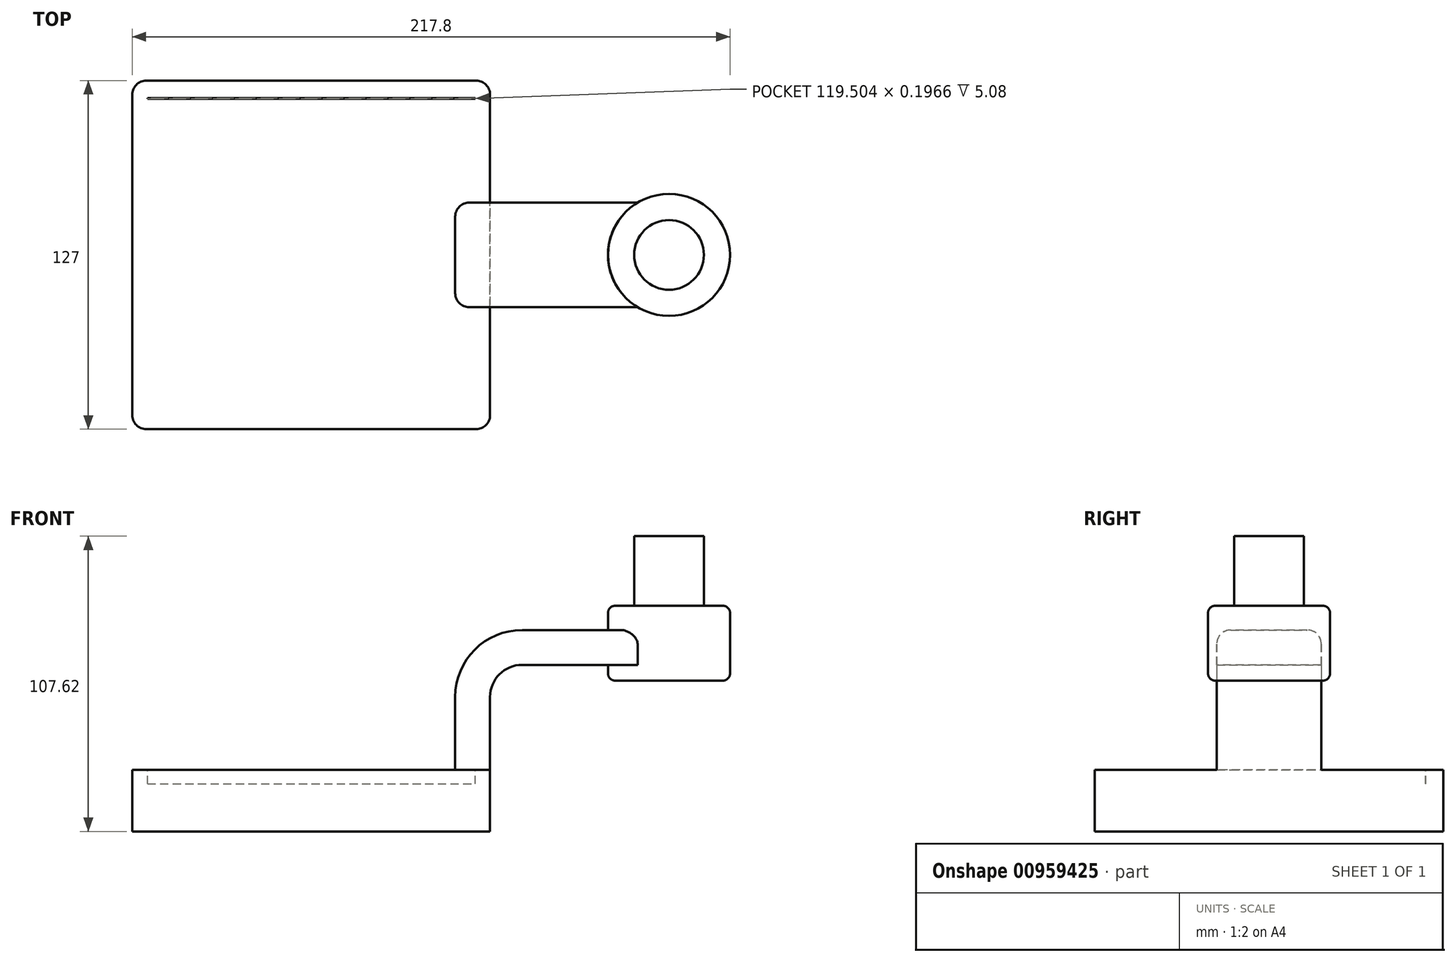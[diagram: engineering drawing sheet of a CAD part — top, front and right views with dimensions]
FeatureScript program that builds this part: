
annotation { "Feature Type Name" : "Feature", "Feature Type Description" : "" }
export const myFeature = defineFeature(function(context is Context, id is Id, definition is map)
    precondition{}
    {
        {
            var Q0;
            Q0=qCreatedBy(makeId("Front.planeOp"),FACE);
            var sketch = newSketch(context, id + "F0", { "sketchPlane" : qUnion([Q0])});
            skLineSegment(sketch, "E0.bottom", {"start": v(-65.2, 11.19) * mm, "end": v(65.2, 11.19) * mm});
            skLineSegment(sketch, "E0.top", {"start": v(-65.2, -11.19) * mm, "end": v(65.2, -11.19) * mm});
            skLineSegment(sketch, "E0.left", {"start": v(-65.2, 11.19) * mm, "end": v(-65.2, -11.19) * mm});
            skLineSegment(sketch, "E0.right", {"start": v(65.2, 11.19) * mm, "end": v(65.2, -11.19) * mm});
            skPoint(sketch, "E0.middle", {"position": v(0, 0) * mm});
            skLineSegment(sketch, "E1.bottom", {"start": v(152.61, 43.79) * mm, "end": v(108.16, 43.79) * mm});
            skLineSegment(sketch, "E1.top", {"start": v(152.61, 71.03) * mm, "end": v(108.16, 71.03) * mm});
            skLineSegment(sketch, "E1.left", {"start": v(152.61, 43.79) * mm, "end": v(152.61, 71.03) * mm});
            skLineSegment(sketch, "E1.right", {"start": v(108.16, 43.79) * mm, "end": v(108.16, 71.03) * mm});
            skPoint(sketch, "E1.middle", {"position": v(130.39, 57.4) * mm});
            skLineSegment(sketch, "E2", {"start": v(65.2, 11.19) * mm, "end": v(65.2, 37.82) * mm});
            skArc(sketch, "E3", {"start": v(65.2, 37.82) * mm, "mid": v(68.62, 46.09) * mm, "end": v(76.88, 49.51) * mm});
            skLineSegment(sketch, "E4", {"start": v(76.88, 49.51) * mm, "end": v(130.39, 49.51) * mm});
            skLineSegment(sketch, "E5.0", {"start": v(76.88, 62.21) * mm, "end": v(130.39, 62.21) * mm});
            skArc(sketch, "E5.1", {"start": v(52.5, 37.82) * mm, "mid": v(59.64, 55.07) * mm, "end": v(76.88, 62.21) * mm});
            skLineSegment(sketch, "E5.2", {"start": v(52.5, 11.19) * mm, "end": v(52.5, 37.82) * mm});
            skFitSpline(sketch, "E6", {"points": [v(-65.2, 11.19) * mm, v(76.88, 62.21) * mm], "startDerivative": vector(116.76, 89.03) * mm, "endDerivative": vector(159.12, -1.65) * mm});
            skPoint(sketch, "E7", {"position": v(130.39, 71.03) * mm});
            skPoint(sketch, "E8", {"position": v(130.39, 43.79) * mm});
            skLineSegment(sketch, "E9", {"start": v(130.39, 71.03) * mm, "end": v(130.39, 43.79) * mm});
            skSolve(sketch);
        }
        {
            var Q0;
            Q0=makeQuery(id+"F0.imprint","IMPRINT",FACE,{"disambiguationData":[TD([[makeQuery(id+"F0.imprint","IMPRINT",EDGE,{"derivedFrom":sQuery(id+"F0.wireOp",EDGE,"E0.top")}),1.0]])]});
            extrude(context, id + "F1", {"entities" : qUnion([Q0]), "endBound" : BoundingType.SYMMETRIC, "oppositeDirection" : true, "depth" : 127 * mm, "offsetDistance" : 25.4 * mm});
        }
        {
            var Q0;
            {var subQ1=sQuery(id+"F0.wireOp",EDGE,"E2");Q0=makeQuery(id+"F0.imprint","IMPRINT",FACE,{"disambiguationData":[TD([[makeQuery(id+"F0.imprint","IMPRINT",EDGE,{"derivedFrom":subQ1}),1.0]])]});}
            var Q1;
            {var subQ0=sQuery(id+"F0.wireOp",EDGE,"E4");var subQ1=sQuery(id+"F0.wireOp",EDGE,"E1.right");var subQ2=makeQuery(id+"F0.imprint","INTERSECT",VERTEX,{"derivedFrom":[subQ1,subQ0]});Q1=makeQuery(id+"F0.imprint","IMPRINT",FACE,{"disambiguationData":[TD([[makeQuery(id+"F0.imprint","IMPRINT",EDGE,{"disambiguationData":[TD([[subQ2,-1.0]])],"derivedFrom":subQ1}),-1.0]])]});}
            extrude(context, id + "F2", {"entities" : qUnion([Q0, Q1]), "operationType" : NewBodyOperationType.ADD, "endBound" : BoundingType.SYMMETRIC, "depth" : 38.1 * mm, "offsetDistance" : 25.4 * mm});
        }
        {
            var Q0;
            Q0=makeQuery(id+"F0.imprint","IMPRINT",FACE,{"disambiguationData":[TD([[makeQuery(id+"F0.imprint","IMPRINT",EDGE,{"derivedFrom":sQuery(id+"F0.wireOp",EDGE,"E5.1")}),1.0]])]});
            var Q1;
            {var subQ0=sQuery(id+"F0.wireOp",EDGE,"E4");var subQ1=sQuery(id+"F0.wireOp",EDGE,"E1.right");var subQ2=makeQuery(id+"F0.imprint","INTERSECT",VERTEX,{"derivedFrom":[subQ1,subQ0]});Q1=makeQuery(id+"F0.imprint","IMPRINT",FACE,{"disambiguationData":[TD([[makeQuery(id+"F0.imprint","IMPRINT",EDGE,{"disambiguationData":[TD([[subQ2,-1.0]])],"derivedFrom":subQ1}),-1.0]])]});}
            extrude(context, id + "F3", {"entities" : qUnion([Q0, Q1]), "operationType" : NewBodyOperationType.ADD, "endBound" : BoundingType.SYMMETRIC, "depth" : 6.35 * mm, "offsetDistance" : 25.4 * mm});
        }
        {
            var Q0;
            {var subQ0=sQuery(id+"F0.wireOp",EDGE,"E1.left");Q0=makeQuery(id+"F0.imprint","IMPRINT",FACE,{"disambiguationData":[TD([[makeQuery(id+"F0.imprint","IMPRINT",EDGE,{"derivedFrom":subQ0}),1.0]])]});}
            var Q1;
            Q1=sQuery(id+"F0.wireOp",EDGE,"E9");
            revolve(context, id + "F4", {"operationType" : NewBodyOperationType.ADD, "surfaceOperationType" : NewSurfaceOperationType.NEW, "entities" : qUnion([Q0]), "axis" : qUnion([Q1]), "revolveType" : RevolveType.FULL});
        }
        {
            var Q0;
            Q0=makeQuery(id+"F1.opExtrude","CAP_EDGE",EDGE,{"disambiguationData":[OSD([sQuery(id+"F0.wireOp",EDGE,"E0.left")])],"isStart":true});
            var Q1;
            Q1=makeQuery(id+"F1.opExtrude","CAP_EDGE",EDGE,{"disambiguationData":[OSD([sQuery(id+"F0.wireOp",EDGE,"E0.right")])],"isStart":true});
            var Q2;
            Q2=makeQuery(id+"F1.opExtrude","CAP_EDGE",EDGE,{"disambiguationData":[OSD([sQuery(id+"F0.wireOp",EDGE,"E0.right")])],"isStart":false});
            var Q3;
            Q3=makeQuery(id+"F1.opExtrude","CAP_EDGE",EDGE,{"disambiguationData":[OSD([sQuery(id+"F0.wireOp",EDGE,"E0.left")])],"isStart":false});
            var Q4;
            Q4=makeQuery(id+"F2.opExtrude","CAP_EDGE",EDGE,{"disambiguationData":[OSD([sQuery(id+"F0.wireOp",EDGE,"E5.2")])],"isStart":true});
            var Q5;
            Q5=makeQuery(id+"F2.opExtrude","CAP_EDGE",EDGE,{"disambiguationData":[OSD([sQuery(id+"F0.wireOp",EDGE,"E5.2")])],"isStart":false});
            fillet(context, id + "F5", {"entities" : qUnion([Q0, Q1, Q2, Q3, Q4, Q5]), "radius" : 5.08 * mm, "tangentPropagation" : true, "allowEdgeOverflow" : false});
        }
        {
            var Q0;
            Q0=makeQuery(id+"F4.opRevolve","SWEPT_EDGE",EDGE,{"disambiguationData":[OSD([sQuery(id+"F0.wireOp",EDGE,"E1.top"),sQuery(id+"F0.wireOp",EDGE,"E1.left")])]});
            fillet(context, id + "F6", {"entities" : qUnion([Q0]), "radius" : 2.54 * mm, "tangentPropagation" : true, "allowEdgeOverflow" : false});
        }
        {
            var Q0;
            Q0=makeQuery(id+"F4.opRevolve","SWEPT_EDGE",EDGE,{"disambiguationData":[OSD([sQuery(id+"F0.wireOp",EDGE,"E1.bottom"),sQuery(id+"F0.wireOp",EDGE,"E1.left")])]});
            fillet(context, id + "F7", {"entities" : qUnion([Q0]), "radius" : 2.54 * mm, "tangentPropagation" : true, "allowEdgeOverflow" : false});
        }
        {
            var Q0;
            Q0=makeQuery(id+"F4.opRevolve","SWEPT_FACE",FACE,{"disambiguationData":[OSD([sQuery(id+"F0.wireOp",EDGE,"E1.top")])]});
            var sketch = newSketch(context, id + "F8", { "sketchPlane" : qUnion([Q0])});
            skCircle(sketch, "E10", {"center": v(130.39, 0) * mm, "radius": 12.7 * mm});
            skSolve(sketch);
        }
        {
            var Q0;
            Q0=makeQuery(id+"F8.imprint","IMPRINT",FACE,{"disambiguationData":[TD([[makeQuery(id+"F8.imprint","IMPRINT",EDGE,{"derivedFrom":sQuery(id+"F8.wireOp",EDGE,"E10")}),1.0]])]});
            extrude(context, id + "F9", {"entities" : qUnion([Q0]), "operationType" : NewBodyOperationType.ADD, "depth" : 25.4 * mm, "offsetDistance" : 25.4 * mm});
        }
        {
            var Q0;
            {var subQ0=sQuery(id+"F0.wireOp",EDGE,"E0.right");var subQ4=sQuery(id+"F0.wireOp",EDGE,"E0.bottom");var subQ5=sQuery(id+"F0.wireOp",EDGE,"E0.left");Q0=makeQuery(id+"F3.boolean.opBoolean","SPLIT",FACE,{"disambiguationData":[TD([makeQuery(id+"F1.opExtrude","CAP_FACE",FACE,{"disambiguationData":[OSD([subQ4,sQuery(id+"F0.wireOp",EDGE,"E0.top"),subQ5,subQ0])],"isStart":false})])],"derivedFrom":makeQuery(id+"F1.opExtrude","SWEPT_FACE",FACE,{"disambiguationData":[OSD([subQ4])]})});}
            var sketch = newSketch(context, id + "F10", { "sketchPlane" : qUnion([Q0])});
            skLineSegment(sketch, "E11.0", {"start": v(-60.11, 57.15) * mm, "end": v(60.11, 57.15) * mm});
            skLineSegment(sketch, "E12.0", {"start": v(-71.54, 58.42) * mm, "end": v(-71.54, 3.17) * mm});
            skLineSegment(sketch, "E13.0", {"start": v(-59.65, 58.42) * mm, "end": v(-59.65, 3.17) * mm});
            skLineSegment(sketch, "E14.0", {"start": v(-60.11, 56.95) * mm, "end": v(60.11, 56.95) * mm});
            skLineSegment(sketch, "E15.0", {"start": v(59.86, 58.42) * mm, "end": v(59.86, 19.05) * mm});
            skSolve(sketch);
        }
        {
            var Q0;
            {var subQ4=sQuery(id+"F0.wireOp",EDGE,"E0.bottom");var subQ17=sQuery(id+"F10.wireOp",EDGE,"E13.0");var subQ20=makeQuery(id+"F3.opExtrude","CAP_EDGE",EDGE,{"disambiguationData":[OSD([subQ4])],"isStart":true});var subQ21=makeQuery(id+"F10.imprint","INTERSECT",VERTEX,{"derivedFrom":[subQ20,subQ17]});Q0=makeQuery(id+"F10.imprint","IMPRINT",FACE,{"disambiguationData":[TD([[makeQuery(id+"F10.imprint","IMPRINT",EDGE,{"disambiguationData":[TD([[subQ21,1.0]])],"derivedFrom":subQ17}),1.0]])]});}
            extrude(context, id + "F11", {"entities" : qUnion([Q0]), "operationType" : NewBodyOperationType.REMOVE, "oppositeDirection" : true, "depth" : 5.08 * mm, "offsetDistance" : 25.4 * mm});
        }
    });
